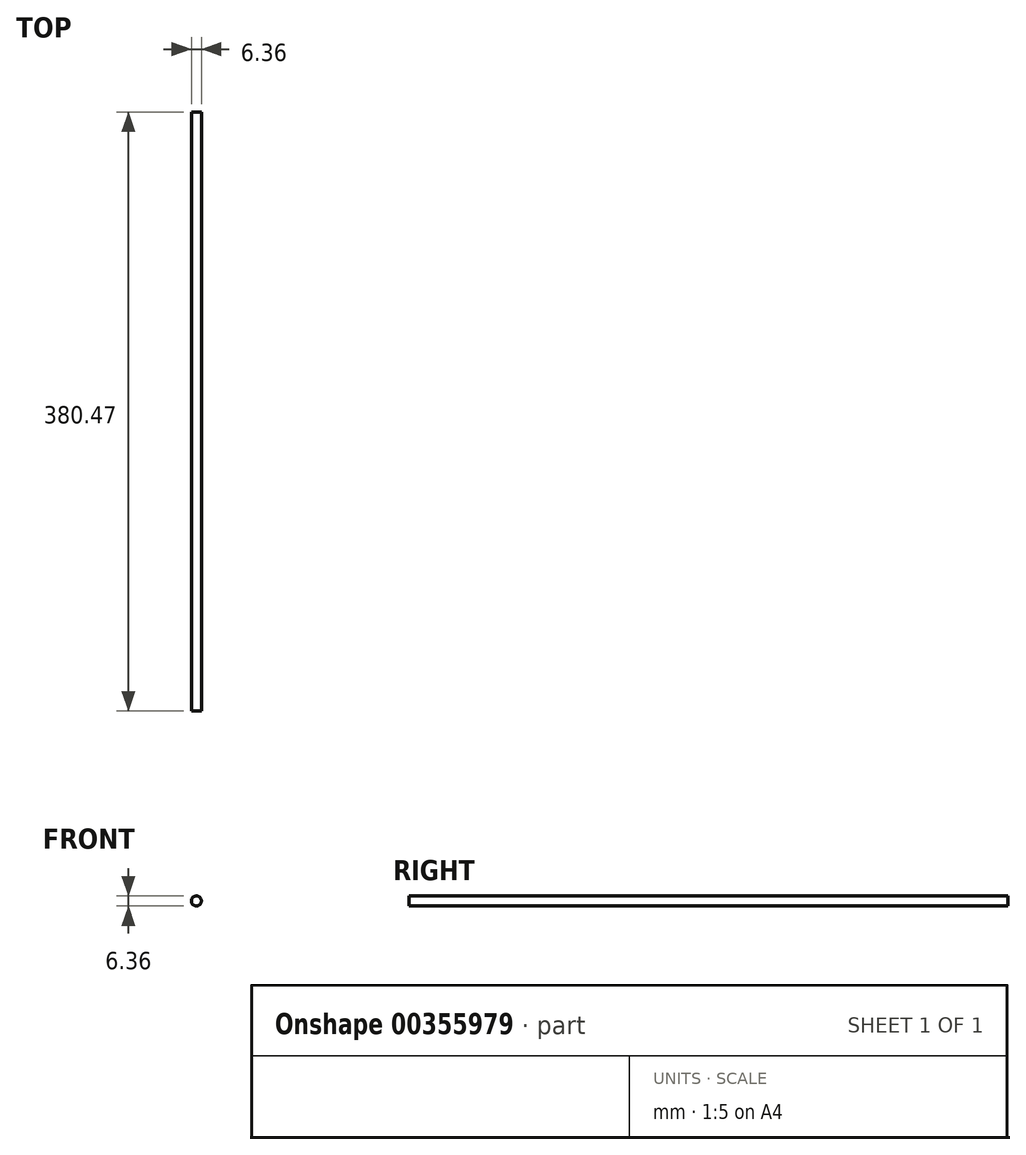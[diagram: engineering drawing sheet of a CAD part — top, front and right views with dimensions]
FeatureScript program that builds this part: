
annotation { "Feature Type Name" : "Feature", "Feature Type Description" : "" }
export const myFeature = defineFeature(function(context is Context, id is Id, definition is map)
    precondition{}
    {
        {
            var Q0;
            Q0=qCreatedBy(makeId("Front.planeOp"),FACE);
            var sketch = newSketch(context, id + "F0", { "sketchPlane" : qUnion([Q0])});
            skCircle(sketch, "E0", {"center": v(0, 0) * mm, "radius": 3.18 * mm});
            skSolve(sketch);
        }
        {
            var Q0;
            Q0=qSketchRegion(id+"F0",true);
            extrude(context, id + "F1", {"entities" : qUnion([Q0]), "depth" : 380.47 * mm});
        }
    });
